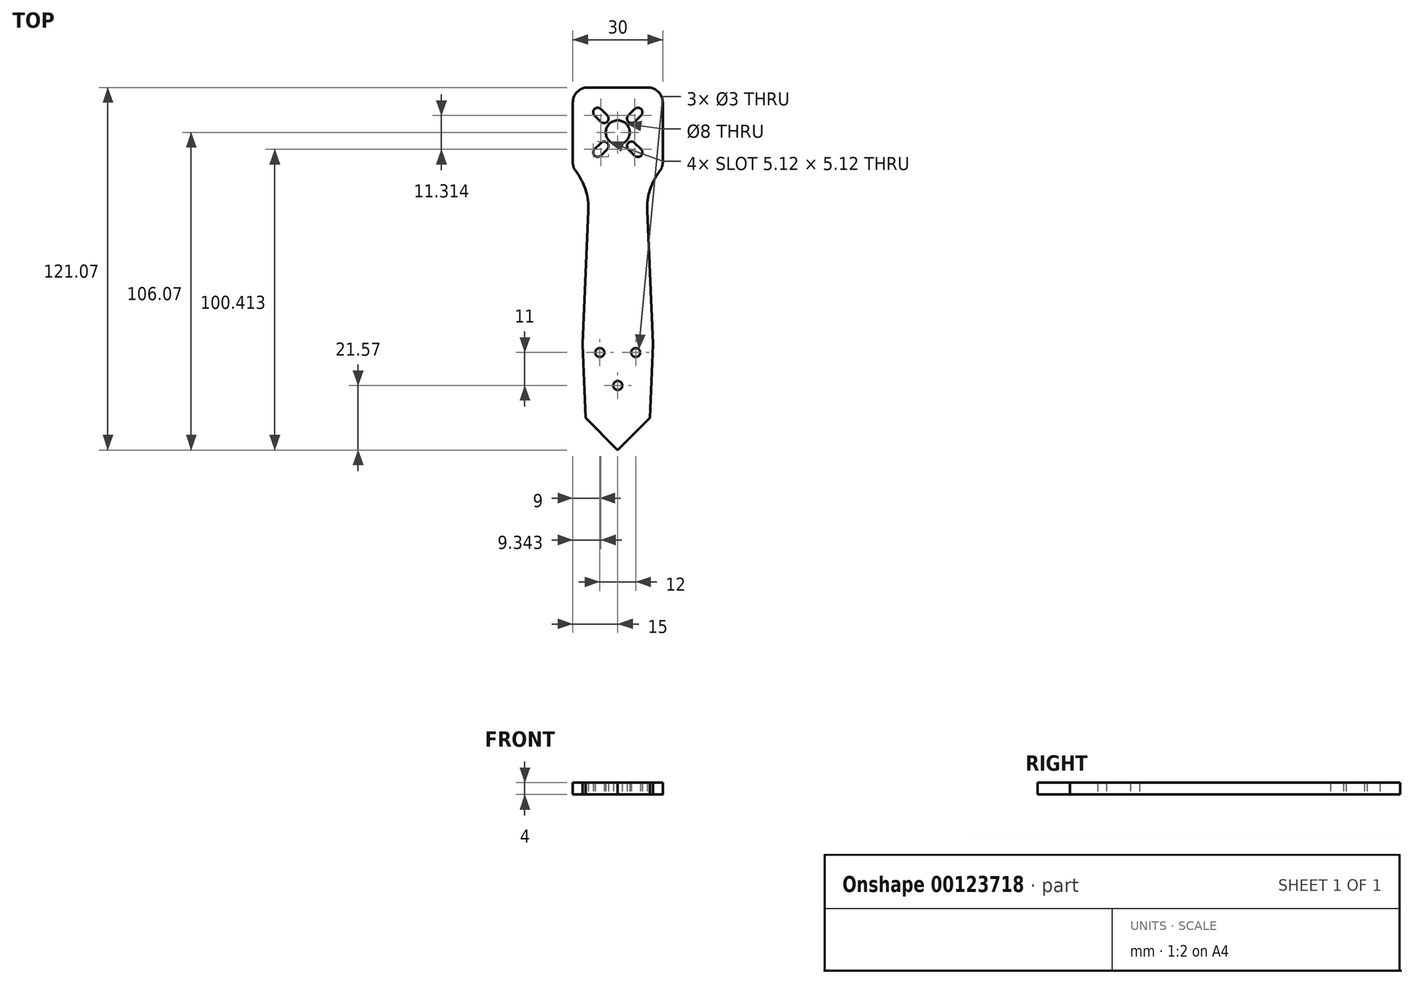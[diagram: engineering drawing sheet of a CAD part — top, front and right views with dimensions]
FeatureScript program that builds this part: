
annotation { "Feature Type Name" : "Feature", "Feature Type Description" : "" }
export const myFeature = defineFeature(function(context is Context, id is Id, definition is map)
    precondition{}
    {
        {
            var Q0;
            Q0=qCreatedBy(makeId("Top.planeOp"),FACE);
            var sketch = newSketch(context, id + "F0", { "sketchPlane" : qUnion([Q0])});
            skCircle(sketch, "E0", {"center": v(0, 0) * mm, "radius": 1.5 * mm});
            skCircle(sketch, "E1", {"center": v(-6, 11) * mm, "radius": 1.5 * mm});
            skCircle(sketch, "E2", {"center": v(6, 11) * mm, "radius": 1.5 * mm});
            skCircle(sketch, "E3", {"center": v(0, 84.5) * mm, "radius": 4 * mm});
            skLineSegment(sketch, "E4", {"start": v(-6, 11) * mm, "end": v(6, 11) * mm, "construction": true});
            skLineSegment(sketch, "E5", {"start": v(-11.75, 14) * mm, "end": v(-9.33, 69.5) * mm});
            skLineSegment(sketch, "E6", {"start": v(11.75, 14) * mm, "end": v(9.33, 69.5) * mm});
            skArc(sketch, "E7.filletArc", {"start": v(-11.75, 14) * mm, "mid": v(-11.75, 13.8) * mm, "end": v(-11.75, 13.58) * mm});
            skArc(sketch, "E8.filletArc", {"start": v(11.75, 13.58) * mm, "mid": v(11.75, 13.8) * mm, "end": v(11.75, 14) * mm});
            skLineSegment(sketch, "E9", {"start": v(-6.72, 77.78) * mm, "end": v(6.72, 91.22) * mm, "construction": true});
            skLineSegment(sketch, "E10", {"start": v(-6.72, 91.22) * mm, "end": v(6.72, 77.78) * mm, "construction": true});
            skArc(sketch, "E11", {"start": v(7.78, 90.16) * mm, "mid": v(7.78, 92.28) * mm, "end": v(5.66, 92.28) * mm});
            skArc(sketch, "E12", {"start": v(-7.78, 78.84) * mm, "mid": v(-7.78, 76.72) * mm, "end": v(-5.66, 76.72) * mm});
            skArc(sketch, "E13", {"start": v(-5.66, 92.28) * mm, "mid": v(-7.78, 92.28) * mm, "end": v(-7.78, 90.16) * mm});
            skArc(sketch, "E14", {"start": v(-5.66, 88.04) * mm, "mid": v(-3.54, 88.04) * mm, "end": v(-3.54, 90.16) * mm});
            skLineSegment(sketch, "E15", {"start": v(5.66, 78.84) * mm, "end": v(5.66, 78.84) * mm});
            skArc(sketch, "E16", {"start": v(5.66, 76.72) * mm, "mid": v(7.78, 76.72) * mm, "end": v(7.78, 78.84) * mm});
            skArc(sketch, "E17", {"start": v(-3.54, 78.84) * mm, "mid": v(-3.54, 80.96) * mm, "end": v(-5.66, 80.96) * mm});
            skArc(sketch, "E18", {"start": v(3.54, 90.16) * mm, "mid": v(3.54, 88.04) * mm, "end": v(5.66, 88.04) * mm});
            skLineSegment(sketch, "E19", {"start": v(-5.66, 92.28) * mm, "end": v(-3.54, 90.16) * mm});
            skLineSegment(sketch, "E20", {"start": v(-7.78, 90.16) * mm, "end": v(-5.66, 88.04) * mm});
            skLineSegment(sketch, "E21", {"start": v(5.66, 92.28) * mm, "end": v(3.54, 90.16) * mm});
            skLineSegment(sketch, "E22", {"start": v(5.66, 88.04) * mm, "end": v(7.78, 90.16) * mm});
            skLineSegment(sketch, "E23", {"start": v(-5.66, 80.96) * mm, "end": v(-7.78, 78.84) * mm});
            skLineSegment(sketch, "E24", {"start": v(-5.66, 76.72) * mm, "end": v(-3.54, 78.84) * mm});
            skLineSegment(sketch, "E25", {"start": v(3.54, 78.84) * mm, "end": v(5.66, 76.72) * mm});
            skLineSegment(sketch, "E26", {"start": v(5.66, 80.96) * mm, "end": v(7.78, 78.84) * mm});
            skArc(sketch, "E27.trimOffspring", {"start": v(5.66, 80.96) * mm, "mid": v(3.54, 80.96) * mm, "end": v(3.54, 78.84) * mm});
            skLineSegment(sketch, "E28.bottom", {"start": v(-10, 99.5) * mm, "end": v(10, 99.5) * mm});
            skLineSegment(sketch, "E28.top", {"start": v(-10, 69.5) * mm, "end": v(-9.33, 69.5) * mm});
            skLineSegment(sketch, "E28.left", {"start": v(-15, 94.5) * mm, "end": v(-15, 74.5) * mm});
            skLineSegment(sketch, "E28.right", {"start": v(15, 94.5) * mm, "end": v(15, 74.5) * mm});
            skLineSegment(sketch, "E29", {"start": v(0, 84.5) * mm, "end": v(-4, 84.5) * mm, "construction": true});
            skLineSegment(sketch, "E30.trimOffspring", {"start": v(9.33, 69.5) * mm, "end": v(10, 69.5) * mm});
            skPoint(sketch, "E31.visualSharp", {"position": v(-15, 99.5) * mm});
            skArc(sketch, "E31.filletArc", {"start": v(-10, 99.5) * mm, "mid": v(-13.54, 98.04) * mm, "end": v(-15, 94.5) * mm});
            skPoint(sketch, "E32.visualSharp", {"position": v(-15, 69.5) * mm});
            skArc(sketch, "E32.filletArc", {"start": v(-15, 74.5) * mm, "mid": v(-13.54, 70.96) * mm, "end": v(-10, 69.5) * mm});
            skPoint(sketch, "E33.visualSharp", {"position": v(15, 69.5) * mm});
            skArc(sketch, "E33.filletArc", {"start": v(10, 69.5) * mm, "mid": v(13.54, 70.96) * mm, "end": v(15, 74.5) * mm});
            skPoint(sketch, "E34.visualSharp", {"position": v(15, 99.5) * mm});
            skArc(sketch, "E34.filletArc", {"start": v(15, 94.5) * mm, "mid": v(13.54, 98.04) * mm, "end": v(10, 99.5) * mm});
            skLineSegment(sketch, "E35", {"start": v(0, 0) * mm, "end": v(21.57, -21.57) * mm, "construction": true});
            skLineSegment(sketch, "E36", {"start": v(21.57, -21.57) * mm, "end": v(0, -43.13) * mm, "construction": true});
            skLineSegment(sketch, "E37", {"start": v(0, -43.13) * mm, "end": v(-21.57, -21.57) * mm, "construction": true});
            skLineSegment(sketch, "E38", {"start": v(-21.57, -21.57) * mm, "end": v(0, 0) * mm, "construction": true});
            skLineSegment(sketch, "E39", {"start": v(-21.57, -21.57) * mm, "end": v(21.57, -21.57) * mm, "construction": true});
            skLineSegment(sketch, "E40", {"start": v(0, -21.57) * mm, "end": v(-10.78, -10.78) * mm});
            skLineSegment(sketch, "E41", {"start": v(0, -21.57) * mm, "end": v(10.78, -10.78) * mm});
            skLineSegment(sketch, "E42", {"start": v(-11.75, 13.58) * mm, "end": v(-10.78, -10.78) * mm});
            skLineSegment(sketch, "E43", {"start": v(10.78, -10.78) * mm, "end": v(11.75, 13.58) * mm});
            skSolve(sketch);
        }
        {
            var Q0;
            Q0=makeQuery(id+"F0.imprint","IMPRINT",FACE,{"disambiguationData":[TD([[makeQuery(id+"F0.imprint","IMPRINT",EDGE,{"derivedFrom":sQuery(id+"F0.wireOp",EDGE,"E0")}),-1.0]])]});
            extrude(context, id + "F1", {"entities" : qUnion([Q0]), "depth" : 4 * mm});
        }
        {
            var Q0;
            Q0=makeQuery(id+"F1.opExtrude","SWEPT_EDGE",EDGE,{"disambiguationData":[OSD([sQuery(id+"F0.wireOp",EDGE,"E5"),sQuery(id+"F0.wireOp",EDGE,"E28.top")])]});
            var Q1;
            Q1=makeQuery(id+"F1.opExtrude","SWEPT_EDGE",EDGE,{"disambiguationData":[OSD([sQuery(id+"F0.wireOp",EDGE,"E6"),sQuery(id+"F0.wireOp",EDGE,"E30.trimOffspring")])]});
            fillet(context, id + "F2", {"entities" : qUnion([Q0, Q1]), "radius" : 20 * mm, "tangentPropagation" : true, "allowEdgeOverflow" : false});
        }
    });
